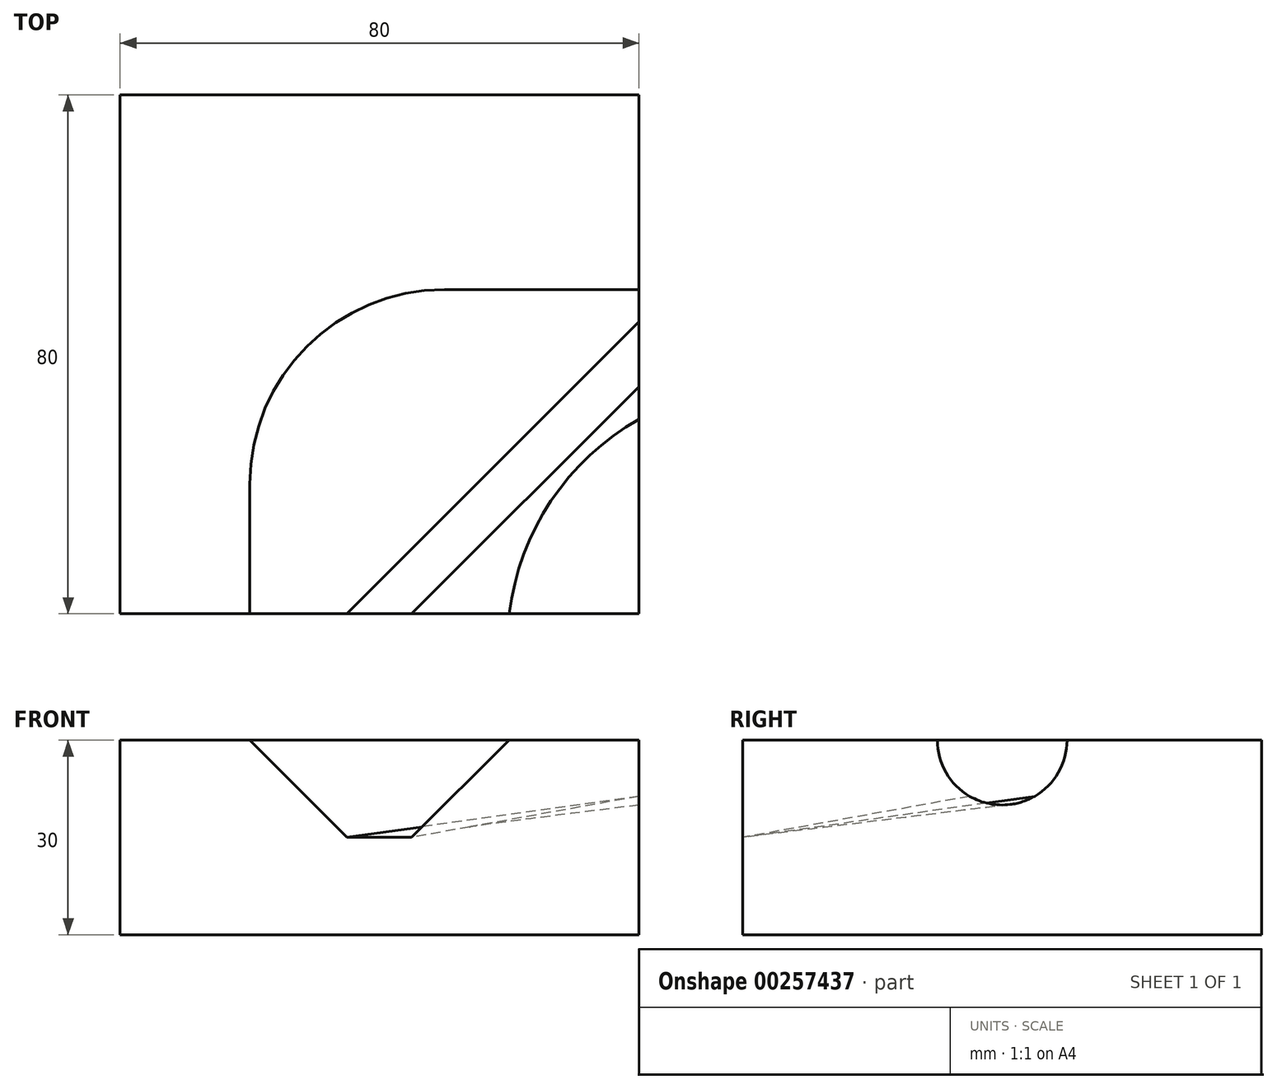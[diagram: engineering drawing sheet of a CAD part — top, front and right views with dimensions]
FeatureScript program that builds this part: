
annotation { "Feature Type Name" : "Feature", "Feature Type Description" : "" }
export const myFeature = defineFeature(function(context is Context, id is Id, definition is map)
    precondition{}
    {
        {
            var Q0;
            Q0=qCreatedBy(makeId("Top.planeOp"),FACE);
            var sketch = newSketch(context, id + "F0", { "sketchPlane" : qUnion([Q0])});
            skLineSegment(sketch, "E0.bottom", {"start": v(-40, 40) * mm, "end": v(40, 40) * mm});
            skLineSegment(sketch, "E0.top", {"start": v(-40, -40) * mm, "end": v(40, -40) * mm});
            skLineSegment(sketch, "E0.left", {"start": v(-40, 40) * mm, "end": v(-40, -40) * mm});
            skLineSegment(sketch, "E0.right", {"start": v(40, 40) * mm, "end": v(40, -40) * mm});
            skPoint(sketch, "E0.middle", {"position": v(0, 0) * mm});
            skSolve(sketch);
        }
        {
            var Q0;
            Q0=makeQuery(id+"F0.imprint","IMPRINT",FACE,{"disambiguationData":[TD([[makeQuery(id+"F0.imprint","IMPRINT",EDGE,{"derivedFrom":sQuery(id+"F0.wireOp",EDGE,"E0.bottom")}),-1.0]])]});
            extrude(context, id + "F1", {"entities" : qUnion([Q0]), "depth" : 30 * mm});
        }
        {
            var Q0;
            Q0=makeQuery(id+"F1.opExtrude","SWEPT_FACE",FACE,{"disambiguationData":[OSD([sQuery(id+"F0.wireOp",EDGE,"E0.right")])]});
            var sketch = newSketch(context, id + "F2", { "sketchPlane" : qUnion([Q0])});
            skPoint(sketch, "E1", {"position": v(0, 30) * mm});
            skArc(sketch, "E2", {"start": v(-10, 30) * mm, "mid": v(0, 20) * mm, "end": v(10, 30) * mm});
            skLineSegment(sketch, "E3.0.0", {"start": v(-40, 0) * mm, "end": v(40, 0) * mm});
            skLineSegment(sketch, "E3.0.1", {"start": v(40, 0) * mm, "end": v(40, 30) * mm});
            skLineSegment(sketch, "E3.0.2", {"start": v(40, 30) * mm, "end": v(-40, 30) * mm});
            skLineSegment(sketch, "E3.0.3", {"start": v(-40, 30) * mm, "end": v(-40, 0) * mm});
            skSolve(sketch);
        }
        {
            var Q0;
            Q0=makeQuery(id+"F1.opExtrude","SWEPT_FACE",FACE,{"disambiguationData":[OSD([sQuery(id+"F0.wireOp",EDGE,"E0.top")])]});
            var sketch = newSketch(context, id + "F3", { "sketchPlane" : qUnion([Q0])});
            skPoint(sketch, "E4.startSnap0", {"position": v(-40, 15) * mm});
            skPoint(sketch, "E5", {"position": v(20, 30) * mm});
            skPoint(sketch, "E6", {"position": v(-20, 30) * mm});
            skLineSegment(sketch, "E7", {"start": v(-5.06, 15) * mm, "end": v(4.94, 15) * mm});
            skLineSegment(sketch, "E8", {"start": v(20, 30) * mm, "end": v(4.94, 15) * mm});
            skLineSegment(sketch, "E9", {"start": v(-20, 30) * mm, "end": v(-5.06, 15) * mm});
            skSolve(sketch);
        }
        {
            var Q0;
            Q0=makeQuery(id+"F1.opExtrude","CAP_FACE",FACE,{"disambiguationData":[OSD([sQuery(id+"F0.wireOp",EDGE,"E0.bottom"),sQuery(id+"F0.wireOp",EDGE,"E0.top"),sQuery(id+"F0.wireOp",EDGE,"E0.left"),sQuery(id+"F0.wireOp",EDGE,"E0.right")])],"isStart":false});
            var sketch = newSketch(context, id + "F4", { "sketchPlane" : qUnion([Q0])});
            skLineSegment(sketch, "E10.0.0", {"start": v(-40, 40) * mm, "end": v(-40, -40) * mm});
            skLineSegment(sketch, "E10.0.1", {"start": v(-40, -40) * mm, "end": v(40, -40) * mm});
            skLineSegment(sketch, "E10.0.2", {"start": v(40, -40) * mm, "end": v(40, 40) * mm});
            skLineSegment(sketch, "E10.0.3", {"start": v(40, 40) * mm, "end": v(-40, 40) * mm});
            skLineSegment(sketch, "E11", {"start": v(40, 10) * mm, "end": v(10, 10) * mm});
            skLineSegment(sketch, "E12", {"start": v(-20, -20) * mm, "end": v(-20, -40) * mm});
            skArc(sketch, "E13", {"start": v(40, -10) * mm, "mid": v(26.43, -22.62) * mm, "end": v(20, -40) * mm});
            skPoint(sketch, "E14.visualSharp", {"position": v(-20, 10) * mm});
            skArc(sketch, "E14.filletArc", {"start": v(10, 10) * mm, "mid": v(-11.21, 1.21) * mm, "end": v(-20, -20) * mm});
            skSolve(sketch);
        }
        {
            var Q0;
            Q0=qCreatedBy(makeId("Top.planeOp"),FACE);
            cPlane(context, id + "F5", {"entities" : qUnion([Q0]), "cplaneType" : CPlaneType.OFFSET, "offset" : 30 * mm, "width" : 150 * mm, "height" : 150 * mm});
        }
        {
            var Q0;
            Q0=qCreatedBy(id+"F5.planeOp",FACE);
            var sketch = newSketch(context, id + "F6", { "sketchPlane" : qUnion([Q0])});
            skLineSegment(sketch, "E15.0", {"start": v(40, 10) * mm, "end": v(10, 10) * mm});
            skArc(sketch, "E16.0", {"start": v(10, 10) * mm, "mid": v(-11.21, 1.21) * mm, "end": v(-20, -20) * mm});
            skLineSegment(sketch, "E17.0", {"start": v(-20, -20) * mm, "end": v(-20, -40) * mm});
            skSolve(sketch);
        }
        {
            var Q1;
            {var subQ0=sQuery(id+"F2.wireOp",EDGE,"E2");Q1=makeQuery(id+"F2.imprint","IMPRINT",FACE,{"disambiguationData":[TD([[makeQuery(id+"F2.imprint","IMPRINT",EDGE,{"derivedFrom":subQ0}),1.0]])]});}
            var Q2;
            Q2=makeQuery(id+"F3.imprint","IMPRINT",FACE,{"disambiguationData":[TD([[makeQuery(id+"F3.imprint","IMPRINT",EDGE,{"derivedFrom":sQuery(id+"F3.wireOp",EDGE,"E7")}),1.0]])]});
            var Q3;
            Q3 = qConstructionFilter(qBodyType(qCreatedBy(id + "F6" ,EDGE), BodyType.WIRE), ConstructionObject.NO);
            var Q4;
            Q4=sQuery(id+"F4.wireOp",EDGE,"E13");
            loft(context, id + "F7", {"operationType" : NewBodyOperationType.REMOVE, "addGuides" : true, "sheetProfilesArray" : [{ "sheetProfileEntities" : qUnion([Q1]) }, { "sheetProfileEntities" : qUnion([Q2]) }], "guidesArray" : [{ "guideEntities" : qUnion([Q3]), "guideDerivativeType" : LoftGuideDerivativeType.DEFAULT, "guideDerivativeMagnitude" : 1 }, { "guideEntities" : qUnion([Q4]), "guideDerivativeType" : LoftGuideDerivativeType.DEFAULT, "guideDerivativeMagnitude" : 1 }]});
        }
    });
